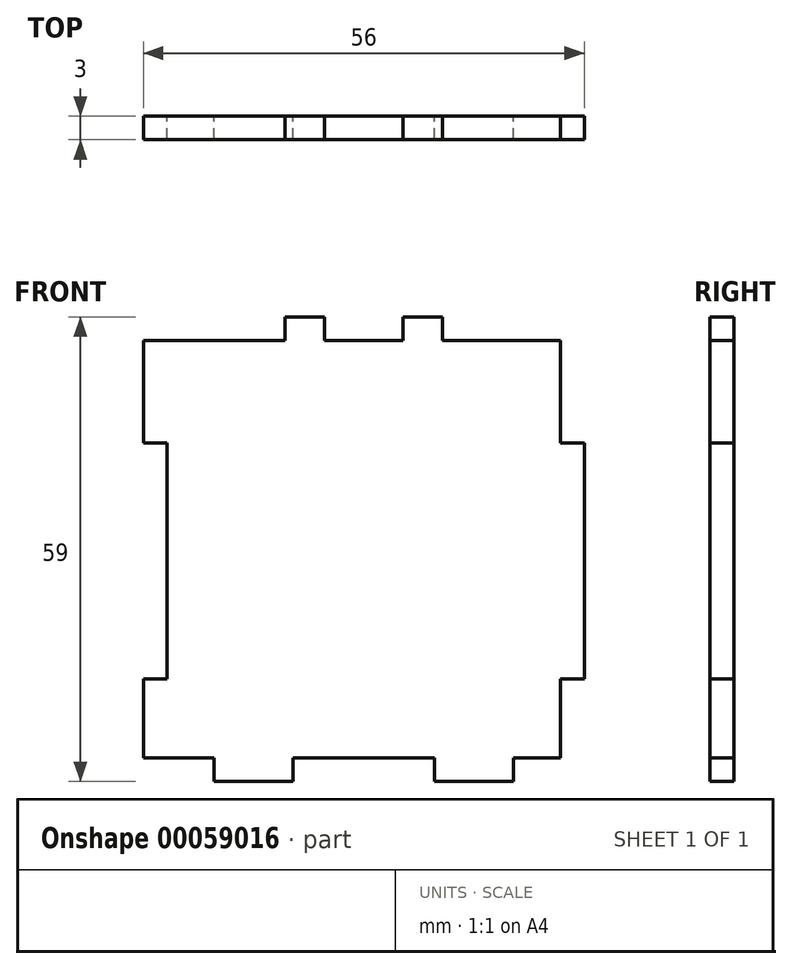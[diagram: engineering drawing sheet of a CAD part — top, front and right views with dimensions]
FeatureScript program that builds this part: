
annotation { "Feature Type Name" : "Feature", "Feature Type Description" : "" }
export const myFeature = defineFeature(function(context is Context, id is Id, definition is map)
    precondition{}
    {
        {
            var Q0;
            Q0=qCreatedBy(makeId("Front.planeOp"),FACE);
            var sketch = newSketch(context, id + "F0", { "sketchPlane" : qUnion([Q0])});
            skLineSegment(sketch, "E0.rect.left", {"start": v(-28, 28) * mm, "end": v(-28, 15) * mm});
            skPoint(sketch, "E0.rect.middle", {"position": v(0, 0) * mm});
            skLineSegment(sketch, "E1.bottom", {"start": v(-28, 15) * mm, "end": v(-25, 15) * mm});
            skLineSegment(sketch, "E1.top", {"start": v(-28, -15) * mm, "end": v(-25, -15) * mm});
            skLineSegment(sketch, "E1.right", {"start": v(-25, 15) * mm, "end": v(-25, -15) * mm});
            skLineSegment(sketch, "E2.trimOffspring", {"start": v(-28, -15) * mm, "end": v(-28, -25) * mm});
            skLineSegment(sketch, "E3", {"start": v(25, 28) * mm, "end": v(25, 15) * mm});
            skLineSegment(sketch, "E4", {"start": v(25, 15) * mm, "end": v(28, 15) * mm});
            skLineSegment(sketch, "E5", {"start": v(28, 15) * mm, "end": v(28, -15) * mm});
            skLineSegment(sketch, "E6", {"start": v(28, -15) * mm, "end": v(25, -15) * mm});
            skLineSegment(sketch, "E7", {"start": v(25, -15) * mm, "end": v(25, -25) * mm});
            skPoint(sketch, "E8.orphan", {"position": v(28, -28) * mm});
            skPoint(sketch, "E9.orphan", {"position": v(28, 28) * mm});
            skLineSegment(sketch, "E10.left", {"start": v(-19, -28) * mm, "end": v(-19, -25) * mm});
            skLineSegment(sketch, "E10.right", {"start": v(19, -28) * mm, "end": v(19, -25) * mm});
            skLineSegment(sketch, "E11", {"start": v(-19, -25) * mm, "end": v(-28, -25) * mm});
            skLineSegment(sketch, "E12", {"start": v(19, -25) * mm, "end": v(25, -25) * mm});
            skPoint(sketch, "E13.orphan", {"position": v(-28, -28) * mm});
            skLineSegment(sketch, "E14", {"start": v(-19, -28) * mm, "end": v(-9, -28) * mm});
            skLineSegment(sketch, "E15", {"start": v(-9, -28) * mm, "end": v(-9, -25) * mm});
            skLineSegment(sketch, "E16", {"start": v(19, -28) * mm, "end": v(9, -28) * mm});
            skLineSegment(sketch, "E17", {"start": v(9, -28) * mm, "end": v(9, -25) * mm});
            skLineSegment(sketch, "E18", {"start": v(-9, -25) * mm, "end": v(9, -25) * mm});
            skLineSegment(sketch, "E19", {"start": v(-25, 15) * mm, "end": v(25, 15) * mm, "construction": true});
            skLineSegment(sketch, "E20.bottom", {"start": v(-10, 31) * mm, "end": v(-5, 31) * mm});
            skLineSegment(sketch, "E20.left", {"start": v(-10, 31) * mm, "end": v(-10, 28) * mm});
            skLineSegment(sketch, "E20.right", {"start": v(-5, 31) * mm, "end": v(-5, 28) * mm});
            skLineSegment(sketch, "E21.MirrorCS", {"start": v(10, 31) * mm, "end": v(5, 31) * mm});
            skLineSegment(sketch, "E22.MirrorCS", {"start": v(5, 31) * mm, "end": v(5, 28) * mm});
            skLineSegment(sketch, "E23.MirrorCS", {"start": v(10, 31) * mm, "end": v(10, 28) * mm});
            skLineSegment(sketch, "E24.trimOffspring", {"start": v(-5, 28) * mm, "end": v(5, 28) * mm});
            skLineSegment(sketch, "E25.trimOffspring", {"start": v(10, 28) * mm, "end": v(25, 28) * mm});
            skLineSegment(sketch, "E26", {"start": v(-10, 28) * mm, "end": v(-28, 28) * mm});
            skSolve(sketch);
        }
        {
            var Q0;
            Q0=makeQuery(id+"F0.imprint","IMPRINT",FACE,{"disambiguationData":[TD([[makeQuery(id+"F0.imprint","IMPRINT",EDGE,{"derivedFrom":sQuery(id+"F0.wireOp",EDGE,"E0.rect.left")}),1.0]])]});
            extrude(context, id + "F1", {"entities" : qUnion([Q0]), "depth" : 3 * mm});
        }
    });
